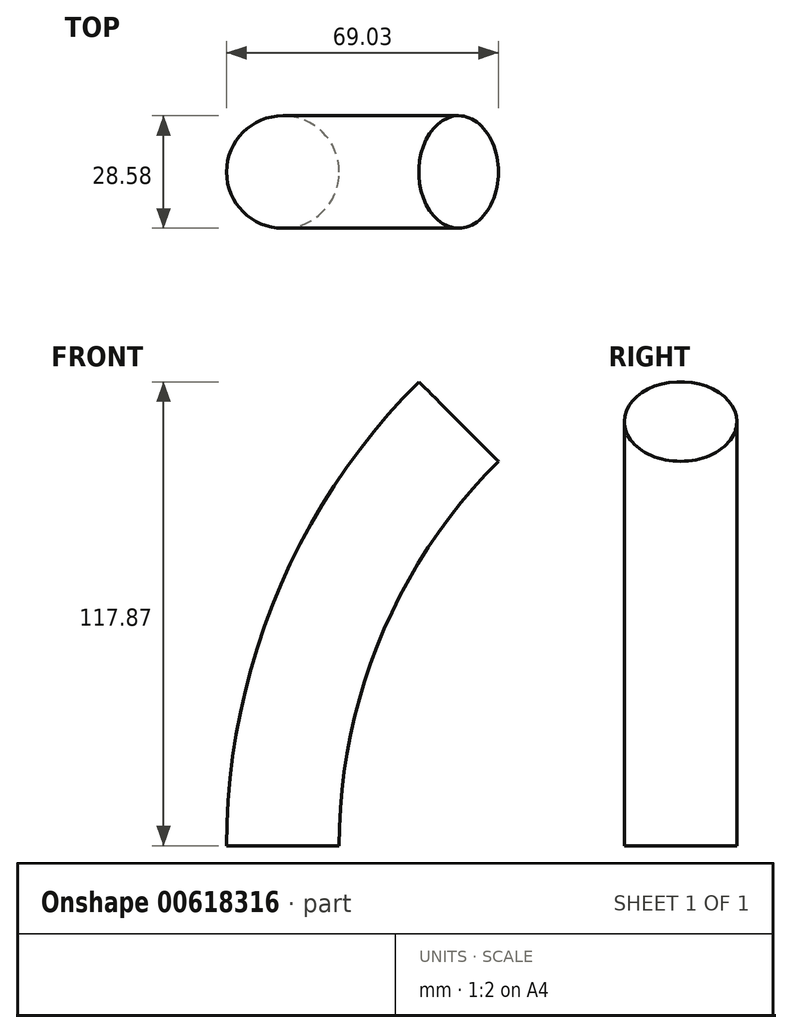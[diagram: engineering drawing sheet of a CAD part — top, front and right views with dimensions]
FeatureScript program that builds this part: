
annotation { "Feature Type Name" : "Feature", "Feature Type Description" : "" }
export const myFeature = defineFeature(function(context is Context, id is Id, definition is map)
    precondition{}
    {
        {
            var Q0;
            Q0=qCreatedBy(makeId("Top.planeOp"),FACE);
            var sketch = newSketch(context, id + "F0", { "sketchPlane" : qUnion([Q0])});
            skLineSegment(sketch, "E0", {"start": v(0, 156.97) * mm, "end": v(0, 0) * mm});
            skLineSegment(sketch, "E1", {"start": v(0, 0) * mm, "end": v(0, -158.22) * mm});
            skLineSegment(sketch, "E2", {"start": v(0, 0) * mm, "end": v(-152.4, 0) * mm});
            skCircle(sketch, "E3", {"center": v(-152.4, 0) * mm, "radius": 14.29 * mm});
            skSolve(sketch);
        }
        {
            var Q0;
            Q0=makeQuery(id+"F0.imprint","IMPRINT",FACE,{"disambiguationData":[TD([[makeQuery(id+"F0.imprint","IMPRINT",EDGE,{"derivedFrom":sQuery(id+"F0.wireOp",EDGE,"E3")}),1.0]])]});
            var Q1;
            Q1=sQuery(id+"F0.wireOp",EDGE,"E1");
            revolve(context, id + "F1", {"entities" : qUnion([Q0]), "axis" : qUnion([Q1]), "revolveType" : RevolveType.ONE_DIRECTION, "oppositeDirection" : true, "angle" : 45 * degree});
        }
    });
